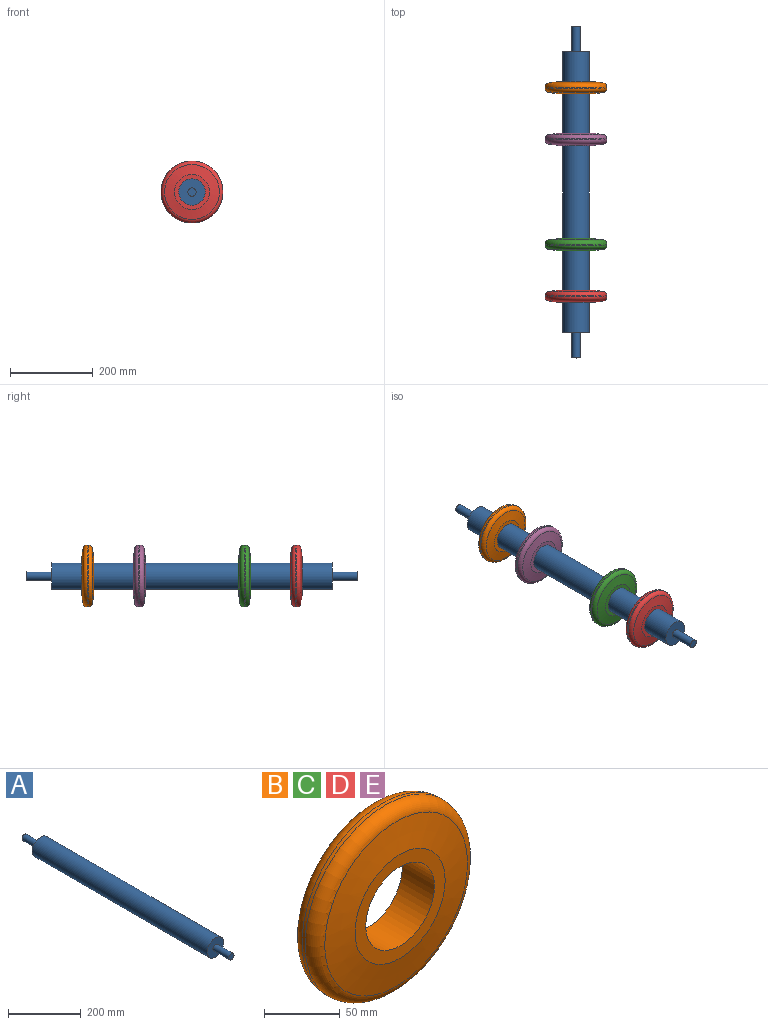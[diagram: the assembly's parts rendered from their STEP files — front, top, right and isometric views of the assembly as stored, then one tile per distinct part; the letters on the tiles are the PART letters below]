
ASSEMBLY  parts=5 mates=4
PART A: 7 faces, bbox 64x804x64 mm
  f0: cylinder r=32mm len=680mm, axis (0,1,0), area 136722.1mm2, adj f1,f2
  f1: plane 64x64mm, normal (0,-1,0), area 2902.8mm2, adj f0,f5
  f2: plane 64x64mm, normal (0,1,0), area 2902.8mm2, adj f0,f4
  f3: plane 20x20mm, normal (0,1,0), area 314.2mm2, adj f4
  f4: cylinder r=10mm len=62mm, axis (0,1,0), area 3895.6mm2, adj f2,f3
  f5: cylinder r=10mm len=62mm, axis (0,1,0), area 3895.6mm2, adj f1,f6
  f6: plane 20x20mm, normal (0,-1,0), area 314.2mm2, adj f5
PART B: 8 faces, bbox 162.4x30x162.4 mm
  f0: cylinder r=32mm len=64mm, axis (0,1,0), area 6031.9mm2, adj f2,f3
  f1: cylinder r=75mm len=150mm, axis (0,1,0), area 1320.4mm2, adj f6,f7
  f2: plane 84x84mm, normal (0,-1,0), area 2324.8mm2, adj f0,f4
  f3: plane 84x84mm, normal (0,1,0), area 2324.8mm2, adj f0,f5
  f4: cone r=42mm half-angle=81.4deg, axis (0,1,0), area 8445.6mm2, adj f2,f6
  f5: cone r=75mm half-angle=81.4deg, axis (0,-1,0), area 8445.6mm2, adj f3,f7
  f6: torus R=65mm, axis (0,-1,0), area 6422.3mm2, adj f1,f4
  f7: torus R=65mm, axis (0,1,0), area 6422.3mm2, adj f1,f5
PART C: same geometry as B
PART D: same geometry as B
PART E: same geometry as B
PLACE A t=(-114.33,177.43,-84.84)mm
PLACE B rot(axis=(1,0,0),180deg) t=(-114.33,74.93,-84.84)mm
PLACE C t=(-114.33,-275.07,-84.84)mm
PLACE D t=(-114.33,-400.07,-84.84)mm
PLACE E rot(axis=(1,0,0),180deg) t=(-114.33,-50.07,-84.84)mm
MATE fastened B.f0 <-> A.f0  axis (0,1,0) through (-114.33,87.43,-84.84)mm
MATE fastened C.f0 <-> A.f0  axis (0,-1,0) through (-114.33,-287.57,-84.84)mm
MATE fastened D.f0 <-> A.f0  axis (0,-1,0) through (-114.33,-412.57,-84.84)mm
MATE fastened E.f0 <-> A.f0  axis (0,1,0) through (-114.33,-37.57,-84.84)mm
